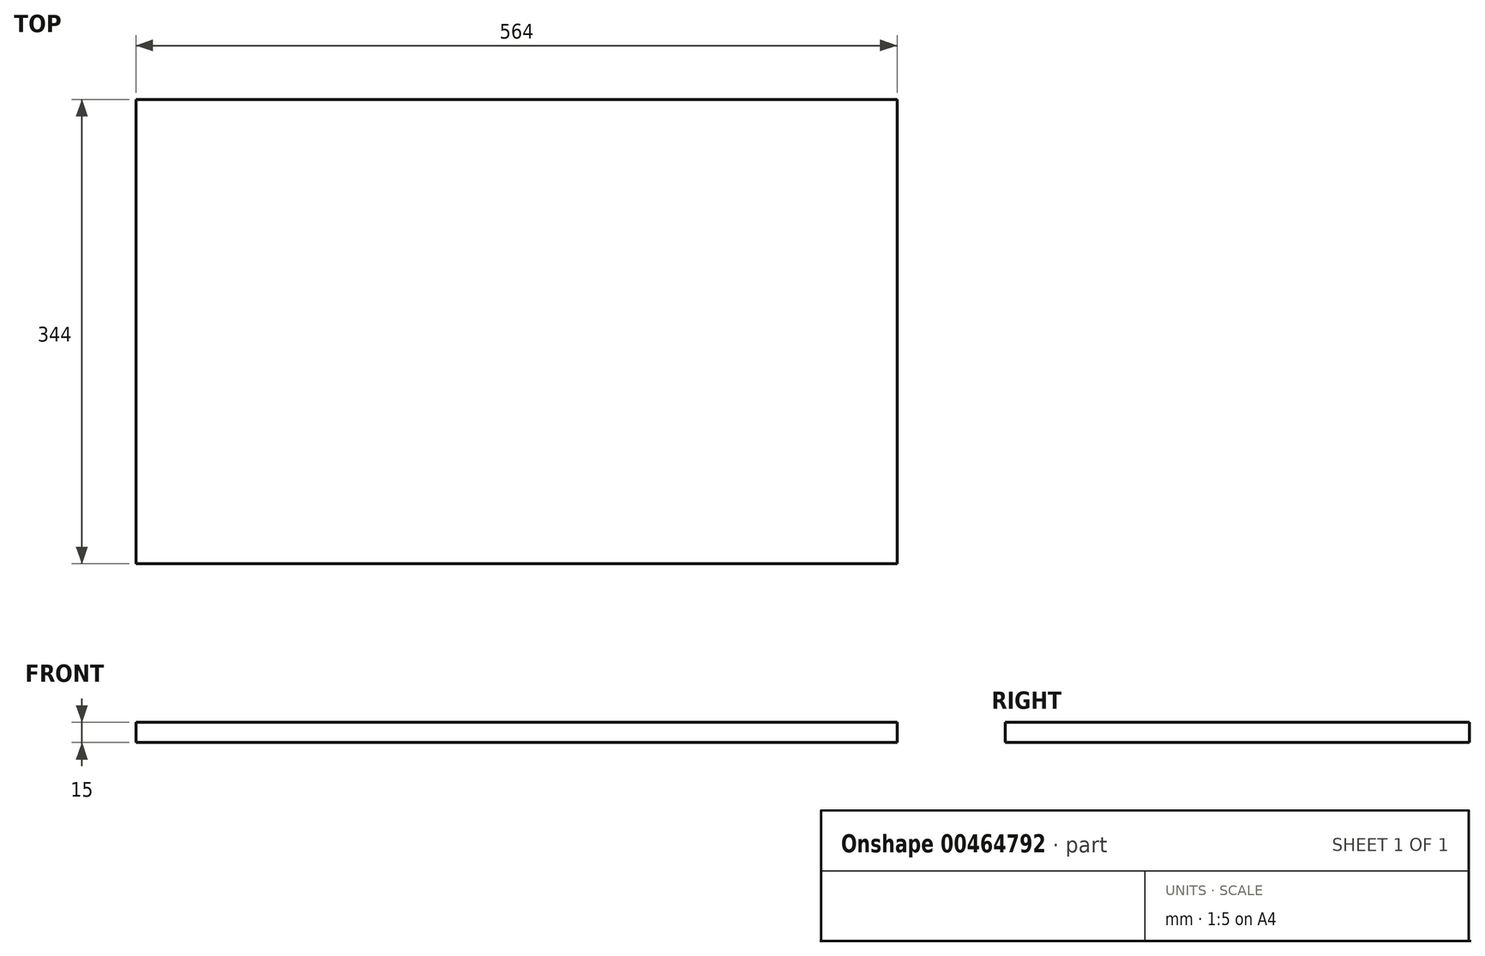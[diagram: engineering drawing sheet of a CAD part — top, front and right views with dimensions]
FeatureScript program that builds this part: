
annotation { "Feature Type Name" : "Feature", "Feature Type Description" : "" }
export const myFeature = defineFeature(function(context is Context, id is Id, definition is map)
    precondition{}
    {
        {
            var Q0;
            Q0=qCreatedBy(makeId("Top.planeOp"),FACE);
            var sketch = newSketch(context, id + "F0", { "sketchPlane" : qUnion([Q0])});
            skLineSegment(sketch, "E0.bottom", {"start": v(0, 0) * mm, "end": v(564, 0) * mm});
            skLineSegment(sketch, "E0.top", {"start": v(0, 344) * mm, "end": v(564, 344) * mm});
            skLineSegment(sketch, "E0.left", {"start": v(0, 0) * mm, "end": v(0, 344) * mm});
            skLineSegment(sketch, "E0.right", {"start": v(564, 0) * mm, "end": v(564, 344) * mm});
            skSolve(sketch);
        }
        {
            var Q0;
            Q0=makeQuery(id+"F0.imprint","IMPRINT",FACE,{"disambiguationData":[TD([[makeQuery(id+"F0.imprint","IMPRINT",EDGE,{"derivedFrom":sQuery(id+"F0.wireOp",EDGE,"E0.bottom")}),1.0]])]});
            extrude(context, id + "F1", {"entities" : qUnion([Q0]), "depth" : 15 * mm});
        }
    });
